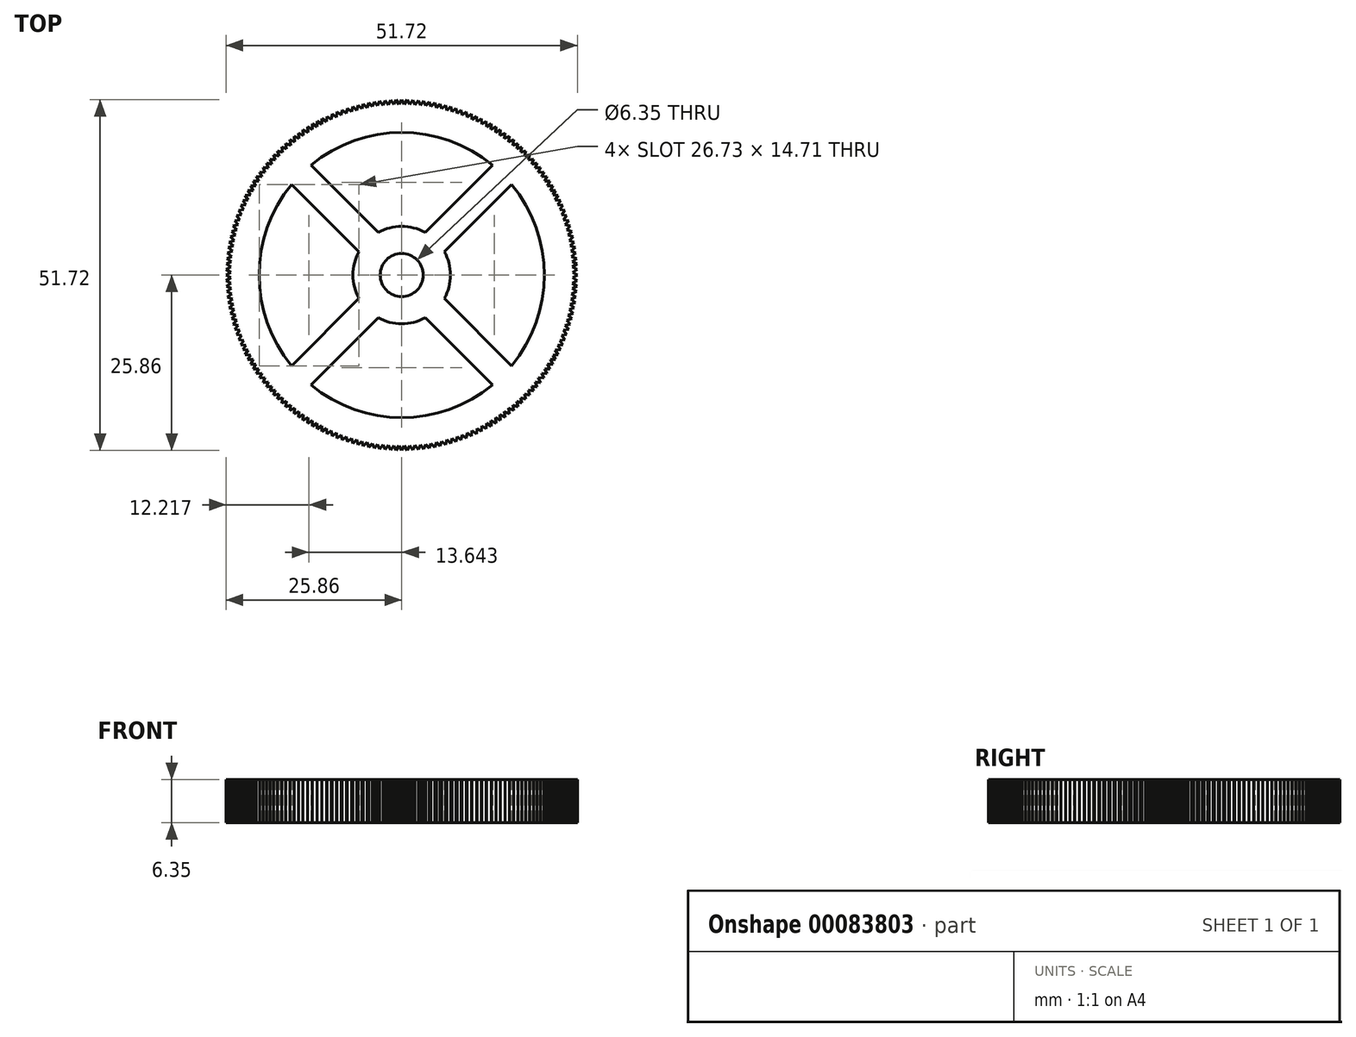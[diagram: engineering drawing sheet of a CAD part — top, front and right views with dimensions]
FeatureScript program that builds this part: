
annotation { "Feature Type Name" : "Feature", "Feature Type Description" : "" }
export const myFeature = defineFeature(function(context is Context, id is Id, definition is map)
    precondition{}
    {
        {
            var Q0;
            Q0=qCreatedBy(makeId("Top.planeOp"),FACE);
            var sketch = newSketch(context, id + "F0", { "sketchPlane" : qUnion([Q0])});
            skCircle(sketch, "E0", {"center": v(0, 0) * mm, "radius": 3.17 * mm});
            skCircle(sketch, "E1", {"center": v(0, 0) * mm, "radius": 25 * mm, "construction": true});
            skLineSegment(sketch, "E2", {"start": v(-3.46, -6.29) * mm, "end": v(-13.37, -16.2) * mm});
            skLineSegment(sketch, "E3", {"start": v(3.46, -6.29) * mm, "end": v(13.37, -16.2) * mm});
            skCircle(sketch, "E4", {"center": v(0, 0) * mm, "radius": 7.17 * mm});
            skCircle(sketch, "E5", {"center": v(0, 0) * mm, "radius": 21 * mm});
            skLineSegment(sketch, "E6.1.0", {"start": v(6.29, 3.46) * mm, "end": v(16.2, 13.37) * mm});
            skLineSegment(sketch, "E6.1.1", {"start": v(6.29, -3.46) * mm, "end": v(16.2, -13.37) * mm});
            skLineSegment(sketch, "E6.2.0", {"start": v(-3.46, 6.29) * mm, "end": v(-13.37, 16.2) * mm});
            skLineSegment(sketch, "E6.2.1", {"start": v(3.46, 6.29) * mm, "end": v(13.37, 16.2) * mm});
            skLineSegment(sketch, "E6.3.0", {"start": v(-6.29, -3.46) * mm, "end": v(-16.2, -13.37) * mm});
            skLineSegment(sketch, "E6.3.1", {"start": v(-6.29, 3.46) * mm, "end": v(-16.2, 13.37) * mm});
            skLineSegment(sketch, "E7", {"start": v(0, -27.54) * mm, "end": v(0, 30.18) * mm, "construction": true});
            skLineSegment(sketch, "E8", {"start": v(-0.5, -25) * mm, "end": v(0, -25.86) * mm});
            skLineSegment(sketch, "E9", {"start": v(0, -25.86) * mm, "end": v(0.5, -25) * mm});
            skLineSegment(sketch, "E10", {"start": v(-0.5, -25) * mm, "end": v(0.5, -25) * mm, "construction": true});
            skLineSegment(sketch, "E11.1.0", {"start": v(0.81, -25.85) * mm, "end": v(1.28, -24.97) * mm});
            skLineSegment(sketch, "E11.1.1", {"start": v(0.29, -25) * mm, "end": v(0.81, -25.85) * mm});
            skLineSegment(sketch, "E11.2.0", {"start": v(1.62, -25.8) * mm, "end": v(2.07, -24.91) * mm});
            skLineSegment(sketch, "E11.2.1", {"start": v(1.07, -24.98) * mm, "end": v(1.62, -25.8) * mm});
            skLineSegment(sketch, "E11.3.0", {"start": v(2.43, -25.75) * mm, "end": v(2.85, -24.84) * mm});
            skLineSegment(sketch, "E11.3.1", {"start": v(1.85, -24.93) * mm, "end": v(2.43, -25.75) * mm});
            skLineSegment(sketch, "E11.4.0", {"start": v(3.24, -25.66) * mm, "end": v(3.63, -24.74) * mm});
            skLineSegment(sketch, "E11.4.1", {"start": v(2.64, -24.86) * mm, "end": v(3.24, -25.66) * mm});
            skLineSegment(sketch, "E11.5.0", {"start": v(4.05, -25.54) * mm, "end": v(4.4, -24.6) * mm});
            skLineSegment(sketch, "E11.5.1", {"start": v(3.42, -24.77) * mm, "end": v(4.05, -25.54) * mm});
            skLineSegment(sketch, "E11.6.0", {"start": v(4.85, -25.4) * mm, "end": v(5.17, -24.46) * mm});
            skLineSegment(sketch, "E11.6.1", {"start": v(4.2, -24.65) * mm, "end": v(4.85, -25.4) * mm});
            skLineSegment(sketch, "E11.7.0", {"start": v(5.64, -25.24) * mm, "end": v(5.94, -24.28) * mm});
            skLineSegment(sketch, "E11.7.1", {"start": v(4.96, -24.5) * mm, "end": v(5.64, -25.24) * mm});
            skLineSegment(sketch, "E11.8.0", {"start": v(6.43, -25.05) * mm, "end": v(6.7, -24.09) * mm});
            skLineSegment(sketch, "E11.8.1", {"start": v(5.73, -24.33) * mm, "end": v(6.43, -25.05) * mm});
            skLineSegment(sketch, "E11.9.0", {"start": v(7.21, -24.83) * mm, "end": v(7.45, -23.86) * mm});
            skLineSegment(sketch, "E11.9.1", {"start": v(6.5, -24.14) * mm, "end": v(7.21, -24.83) * mm});
            skLineSegment(sketch, "E11.10.0", {"start": v(8, -24.6) * mm, "end": v(8.2, -23.62) * mm});
            skLineSegment(sketch, "E11.10.1", {"start": v(7.25, -23.93) * mm, "end": v(8, -24.6) * mm});
            skLineSegment(sketch, "E11.11.0", {"start": v(8.76, -24.33) * mm, "end": v(8.94, -23.35) * mm});
            skLineSegment(sketch, "E11.11.1", {"start": v(8, -23.69) * mm, "end": v(8.76, -24.33) * mm});
            skLineSegment(sketch, "E11.12.0", {"start": v(9.52, -24.04) * mm, "end": v(9.67, -23.06) * mm});
            skLineSegment(sketch, "E11.12.1", {"start": v(8.74, -23.42) * mm, "end": v(9.52, -24.04) * mm});
            skLineSegment(sketch, "E11.13.0", {"start": v(10.27, -23.73) * mm, "end": v(10.39, -22.74) * mm});
            skLineSegment(sketch, "E11.13.1", {"start": v(9.47, -23.14) * mm, "end": v(10.27, -23.73) * mm});
            skLineSegment(sketch, "E11.14.0", {"start": v(11.01, -23.4) * mm, "end": v(11.1, -22.4) * mm});
            skLineSegment(sketch, "E11.14.1", {"start": v(10.19, -22.83) * mm, "end": v(11.01, -23.4) * mm});
            skLineSegment(sketch, "E11.15.0", {"start": v(11.74, -23.04) * mm, "end": v(11.8, -22.04) * mm});
            skLineSegment(sketch, "E11.15.1", {"start": v(10.9, -22.5) * mm, "end": v(11.74, -23.04) * mm});
            skLineSegment(sketch, "E11.16.0", {"start": v(12.46, -22.66) * mm, "end": v(12.48, -21.66) * mm});
            skLineSegment(sketch, "E11.16.1", {"start": v(11.6, -22.14) * mm, "end": v(12.46, -22.66) * mm});
            skLineSegment(sketch, "E11.17.0", {"start": v(13.16, -22.26) * mm, "end": v(13.15, -21.26) * mm});
            skLineSegment(sketch, "E11.17.1", {"start": v(12.3, -21.77) * mm, "end": v(13.16, -22.26) * mm});
            skLineSegment(sketch, "E11.18.0", {"start": v(13.86, -21.84) * mm, "end": v(13.82, -20.84) * mm});
            skLineSegment(sketch, "E11.18.1", {"start": v(12.97, -21.37) * mm, "end": v(13.86, -21.84) * mm});
            skLineSegment(sketch, "E11.19.0", {"start": v(14.54, -21.39) * mm, "end": v(14.46, -20.4) * mm});
            skLineSegment(sketch, "E11.19.1", {"start": v(13.64, -20.95) * mm, "end": v(14.54, -21.39) * mm});
            skLineSegment(sketch, "E11.20.0", {"start": v(15.2, -20.92) * mm, "end": v(15.1, -19.93) * mm});
            skLineSegment(sketch, "E11.20.1", {"start": v(14.29, -20.52) * mm, "end": v(15.2, -20.92) * mm});
            skLineSegment(sketch, "E11.21.0", {"start": v(15.85, -20.43) * mm, "end": v(15.71, -19.44) * mm});
            skLineSegment(sketch, "E11.21.1", {"start": v(14.92, -20.06) * mm, "end": v(15.85, -20.43) * mm});
            skLineSegment(sketch, "E11.22.0", {"start": v(16.48, -19.93) * mm, "end": v(16.32, -18.94) * mm});
            skLineSegment(sketch, "E11.22.1", {"start": v(15.55, -19.58) * mm, "end": v(16.48, -19.93) * mm});
            skLineSegment(sketch, "E11.23.0", {"start": v(17.1, -19.4) * mm, "end": v(16.9, -18.42) * mm});
            skLineSegment(sketch, "E11.23.1", {"start": v(16.15, -19.08) * mm, "end": v(17.1, -19.4) * mm});
            skLineSegment(sketch, "E11.24.0", {"start": v(17.7, -18.85) * mm, "end": v(17.47, -17.88) * mm});
            skLineSegment(sketch, "E11.24.1", {"start": v(16.75, -18.56) * mm, "end": v(17.7, -18.85) * mm});
            skLineSegment(sketch, "E11.25.0", {"start": v(18.29, -18.29) * mm, "end": v(18.03, -17.32) * mm});
            skLineSegment(sketch, "E11.25.1", {"start": v(17.32, -18.03) * mm, "end": v(18.29, -18.29) * mm});
            skLineSegment(sketch, "E11.26.0", {"start": v(18.85, -17.7) * mm, "end": v(18.56, -16.75) * mm});
            skLineSegment(sketch, "E11.26.1", {"start": v(17.88, -17.47) * mm, "end": v(18.85, -17.7) * mm});
            skLineSegment(sketch, "E11.27.0", {"start": v(19.4, -17.1) * mm, "end": v(19.08, -16.15) * mm});
            skLineSegment(sketch, "E11.27.1", {"start": v(18.42, -16.9) * mm, "end": v(19.4, -17.1) * mm});
            skLineSegment(sketch, "E11.28.0", {"start": v(19.93, -16.48) * mm, "end": v(19.58, -15.55) * mm});
            skLineSegment(sketch, "E11.28.1", {"start": v(18.94, -16.32) * mm, "end": v(19.93, -16.48) * mm});
            skLineSegment(sketch, "E11.29.0", {"start": v(20.43, -15.85) * mm, "end": v(20.06, -14.92) * mm});
            skLineSegment(sketch, "E11.29.1", {"start": v(19.44, -15.71) * mm, "end": v(20.43, -15.85) * mm});
            skLineSegment(sketch, "E11.30.0", {"start": v(20.92, -15.2) * mm, "end": v(20.52, -14.29) * mm});
            skLineSegment(sketch, "E11.30.1", {"start": v(19.93, -15.1) * mm, "end": v(20.92, -15.2) * mm});
            skLineSegment(sketch, "E11.31.0", {"start": v(21.39, -14.54) * mm, "end": v(20.95, -13.64) * mm});
            skLineSegment(sketch, "E11.31.1", {"start": v(20.4, -14.46) * mm, "end": v(21.39, -14.54) * mm});
            skLineSegment(sketch, "E11.32.0", {"start": v(21.84, -13.86) * mm, "end": v(21.37, -12.97) * mm});
            skLineSegment(sketch, "E11.32.1", {"start": v(20.84, -13.82) * mm, "end": v(21.84, -13.86) * mm});
            skLineSegment(sketch, "E11.33.0", {"start": v(22.26, -13.16) * mm, "end": v(21.77, -12.3) * mm});
            skLineSegment(sketch, "E11.33.1", {"start": v(21.26, -13.15) * mm, "end": v(22.26, -13.16) * mm});
            skLineSegment(sketch, "E11.34.0", {"start": v(22.66, -12.46) * mm, "end": v(22.14, -11.6) * mm});
            skLineSegment(sketch, "E11.34.1", {"start": v(21.66, -12.48) * mm, "end": v(22.66, -12.46) * mm});
            skLineSegment(sketch, "E11.35.0", {"start": v(23.04, -11.74) * mm, "end": v(22.5, -10.9) * mm});
            skLineSegment(sketch, "E11.35.1", {"start": v(22.04, -11.8) * mm, "end": v(23.04, -11.74) * mm});
            skLineSegment(sketch, "E11.36.0", {"start": v(23.4, -11.01) * mm, "end": v(22.83, -10.19) * mm});
            skLineSegment(sketch, "E11.36.1", {"start": v(22.4, -11.1) * mm, "end": v(23.4, -11.01) * mm});
            skLineSegment(sketch, "E11.37.0", {"start": v(23.73, -10.27) * mm, "end": v(23.14, -9.47) * mm});
            skLineSegment(sketch, "E11.37.1", {"start": v(22.74, -10.39) * mm, "end": v(23.73, -10.27) * mm});
            skLineSegment(sketch, "E11.38.0", {"start": v(24.04, -9.52) * mm, "end": v(23.42, -8.74) * mm});
            skLineSegment(sketch, "E11.38.1", {"start": v(23.06, -9.67) * mm, "end": v(24.04, -9.52) * mm});
            skLineSegment(sketch, "E11.39.0", {"start": v(24.33, -8.76) * mm, "end": v(23.69, -8) * mm});
            skLineSegment(sketch, "E11.39.1", {"start": v(23.35, -8.94) * mm, "end": v(24.33, -8.76) * mm});
            skLineSegment(sketch, "E11.40.0", {"start": v(24.6, -8) * mm, "end": v(23.93, -7.25) * mm});
            skLineSegment(sketch, "E11.40.1", {"start": v(23.62, -8.2) * mm, "end": v(24.6, -8) * mm});
            skLineSegment(sketch, "E11.41.0", {"start": v(24.83, -7.21) * mm, "end": v(24.14, -6.5) * mm});
            skLineSegment(sketch, "E11.41.1", {"start": v(23.86, -7.45) * mm, "end": v(24.83, -7.21) * mm});
            skLineSegment(sketch, "E11.42.0", {"start": v(25.05, -6.43) * mm, "end": v(24.33, -5.73) * mm});
            skLineSegment(sketch, "E11.42.1", {"start": v(24.09, -6.7) * mm, "end": v(25.05, -6.43) * mm});
            skLineSegment(sketch, "E11.43.0", {"start": v(25.24, -5.64) * mm, "end": v(24.5, -4.96) * mm});
            skLineSegment(sketch, "E11.43.1", {"start": v(24.28, -5.94) * mm, "end": v(25.24, -5.64) * mm});
            skLineSegment(sketch, "E11.44.0", {"start": v(25.4, -4.85) * mm, "end": v(24.65, -4.2) * mm});
            skLineSegment(sketch, "E11.44.1", {"start": v(24.46, -5.17) * mm, "end": v(25.4, -4.85) * mm});
            skLineSegment(sketch, "E11.45.0", {"start": v(25.54, -4.05) * mm, "end": v(24.77, -3.42) * mm});
            skLineSegment(sketch, "E11.45.1", {"start": v(24.6, -4.4) * mm, "end": v(25.54, -4.05) * mm});
            skLineSegment(sketch, "E11.46.0", {"start": v(25.66, -3.24) * mm, "end": v(24.86, -2.64) * mm});
            skLineSegment(sketch, "E11.46.1", {"start": v(24.74, -3.63) * mm, "end": v(25.66, -3.24) * mm});
            skLineSegment(sketch, "E11.47.0", {"start": v(25.75, -2.43) * mm, "end": v(24.93, -1.85) * mm});
            skLineSegment(sketch, "E11.47.1", {"start": v(24.84, -2.85) * mm, "end": v(25.75, -2.43) * mm});
            skLineSegment(sketch, "E11.48.0", {"start": v(25.8, -1.62) * mm, "end": v(24.98, -1.07) * mm});
            skLineSegment(sketch, "E11.48.1", {"start": v(24.91, -2.07) * mm, "end": v(25.8, -1.62) * mm});
            skLineSegment(sketch, "E11.49.0", {"start": v(25.85, -0.81) * mm, "end": v(25, -0.29) * mm});
            skLineSegment(sketch, "E11.49.1", {"start": v(24.97, -1.28) * mm, "end": v(25.85, -0.81) * mm});
            skLineSegment(sketch, "E11.50.0", {"start": v(25.86, 0) * mm, "end": v(25, 0.5) * mm});
            skLineSegment(sketch, "E11.50.1", {"start": v(25, -0.5) * mm, "end": v(25.86, 0) * mm});
            skLineSegment(sketch, "E11.51.0", {"start": v(25.85, 0.81) * mm, "end": v(24.97, 1.28) * mm});
            skLineSegment(sketch, "E11.51.1", {"start": v(25, 0.29) * mm, "end": v(25.85, 0.81) * mm});
            skLineSegment(sketch, "E11.52.0", {"start": v(25.8, 1.62) * mm, "end": v(24.91, 2.07) * mm});
            skLineSegment(sketch, "E11.52.1", {"start": v(24.98, 1.07) * mm, "end": v(25.8, 1.62) * mm});
            skLineSegment(sketch, "E11.53.0", {"start": v(25.75, 2.43) * mm, "end": v(24.84, 2.85) * mm});
            skLineSegment(sketch, "E11.53.1", {"start": v(24.93, 1.85) * mm, "end": v(25.75, 2.43) * mm});
            skLineSegment(sketch, "E11.54.0", {"start": v(25.66, 3.24) * mm, "end": v(24.74, 3.63) * mm});
            skLineSegment(sketch, "E11.54.1", {"start": v(24.86, 2.64) * mm, "end": v(25.66, 3.24) * mm});
            skLineSegment(sketch, "E11.55.0", {"start": v(25.54, 4.05) * mm, "end": v(24.6, 4.4) * mm});
            skLineSegment(sketch, "E11.55.1", {"start": v(24.77, 3.42) * mm, "end": v(25.54, 4.05) * mm});
            skLineSegment(sketch, "E11.56.0", {"start": v(25.4, 4.85) * mm, "end": v(24.46, 5.17) * mm});
            skLineSegment(sketch, "E11.56.1", {"start": v(24.65, 4.2) * mm, "end": v(25.4, 4.85) * mm});
            skLineSegment(sketch, "E11.57.0", {"start": v(25.24, 5.64) * mm, "end": v(24.28, 5.94) * mm});
            skLineSegment(sketch, "E11.57.1", {"start": v(24.5, 4.96) * mm, "end": v(25.24, 5.64) * mm});
            skLineSegment(sketch, "E11.58.0", {"start": v(25.05, 6.43) * mm, "end": v(24.09, 6.7) * mm});
            skLineSegment(sketch, "E11.58.1", {"start": v(24.33, 5.73) * mm, "end": v(25.05, 6.43) * mm});
            skLineSegment(sketch, "E11.59.0", {"start": v(24.83, 7.21) * mm, "end": v(23.86, 7.45) * mm});
            skLineSegment(sketch, "E11.59.1", {"start": v(24.14, 6.5) * mm, "end": v(24.83, 7.21) * mm});
            skLineSegment(sketch, "E11.60.0", {"start": v(24.6, 8) * mm, "end": v(23.62, 8.2) * mm});
            skLineSegment(sketch, "E11.60.1", {"start": v(23.93, 7.25) * mm, "end": v(24.6, 8) * mm});
            skLineSegment(sketch, "E11.61.0", {"start": v(24.33, 8.76) * mm, "end": v(23.35, 8.94) * mm});
            skLineSegment(sketch, "E11.61.1", {"start": v(23.69, 8) * mm, "end": v(24.33, 8.76) * mm});
            skLineSegment(sketch, "E11.62.0", {"start": v(24.04, 9.52) * mm, "end": v(23.06, 9.67) * mm});
            skLineSegment(sketch, "E11.62.1", {"start": v(23.42, 8.74) * mm, "end": v(24.04, 9.52) * mm});
            skLineSegment(sketch, "E11.63.0", {"start": v(23.73, 10.27) * mm, "end": v(22.74, 10.39) * mm});
            skLineSegment(sketch, "E11.63.1", {"start": v(23.14, 9.47) * mm, "end": v(23.73, 10.27) * mm});
            skLineSegment(sketch, "E11.64.0", {"start": v(23.4, 11.01) * mm, "end": v(22.4, 11.1) * mm});
            skLineSegment(sketch, "E11.64.1", {"start": v(22.83, 10.19) * mm, "end": v(23.4, 11.01) * mm});
            skLineSegment(sketch, "E11.65.0", {"start": v(23.04, 11.74) * mm, "end": v(22.04, 11.8) * mm});
            skLineSegment(sketch, "E11.65.1", {"start": v(22.5, 10.9) * mm, "end": v(23.04, 11.74) * mm});
            skLineSegment(sketch, "E11.66.0", {"start": v(22.66, 12.46) * mm, "end": v(21.66, 12.48) * mm});
            skLineSegment(sketch, "E11.66.1", {"start": v(22.14, 11.6) * mm, "end": v(22.66, 12.46) * mm});
            skLineSegment(sketch, "E11.67.0", {"start": v(22.26, 13.16) * mm, "end": v(21.26, 13.15) * mm});
            skLineSegment(sketch, "E11.67.1", {"start": v(21.77, 12.3) * mm, "end": v(22.26, 13.16) * mm});
            skLineSegment(sketch, "E11.68.0", {"start": v(21.84, 13.86) * mm, "end": v(20.84, 13.82) * mm});
            skLineSegment(sketch, "E11.68.1", {"start": v(21.37, 12.97) * mm, "end": v(21.84, 13.86) * mm});
            skLineSegment(sketch, "E11.69.0", {"start": v(21.39, 14.54) * mm, "end": v(20.4, 14.46) * mm});
            skLineSegment(sketch, "E11.69.1", {"start": v(20.95, 13.64) * mm, "end": v(21.39, 14.54) * mm});
            skLineSegment(sketch, "E11.70.0", {"start": v(20.92, 15.2) * mm, "end": v(19.93, 15.1) * mm});
            skLineSegment(sketch, "E11.70.1", {"start": v(20.52, 14.29) * mm, "end": v(20.92, 15.2) * mm});
            skLineSegment(sketch, "E11.71.0", {"start": v(20.43, 15.85) * mm, "end": v(19.44, 15.71) * mm});
            skLineSegment(sketch, "E11.71.1", {"start": v(20.06, 14.92) * mm, "end": v(20.43, 15.85) * mm});
            skLineSegment(sketch, "E11.72.0", {"start": v(19.93, 16.48) * mm, "end": v(18.94, 16.32) * mm});
            skLineSegment(sketch, "E11.72.1", {"start": v(19.58, 15.55) * mm, "end": v(19.93, 16.48) * mm});
            skLineSegment(sketch, "E11.73.0", {"start": v(19.4, 17.1) * mm, "end": v(18.42, 16.9) * mm});
            skLineSegment(sketch, "E11.73.1", {"start": v(19.08, 16.15) * mm, "end": v(19.4, 17.1) * mm});
            skLineSegment(sketch, "E11.74.0", {"start": v(18.85, 17.7) * mm, "end": v(17.88, 17.47) * mm});
            skLineSegment(sketch, "E11.74.1", {"start": v(18.56, 16.75) * mm, "end": v(18.85, 17.7) * mm});
            skLineSegment(sketch, "E11.75.0", {"start": v(18.29, 18.29) * mm, "end": v(17.32, 18.03) * mm});
            skLineSegment(sketch, "E11.75.1", {"start": v(18.03, 17.32) * mm, "end": v(18.29, 18.29) * mm});
            skLineSegment(sketch, "E11.76.0", {"start": v(17.7, 18.85) * mm, "end": v(16.75, 18.56) * mm});
            skLineSegment(sketch, "E11.76.1", {"start": v(17.47, 17.88) * mm, "end": v(17.7, 18.85) * mm});
            skLineSegment(sketch, "E11.77.0", {"start": v(17.1, 19.4) * mm, "end": v(16.15, 19.08) * mm});
            skLineSegment(sketch, "E11.77.1", {"start": v(16.9, 18.42) * mm, "end": v(17.1, 19.4) * mm});
            skLineSegment(sketch, "E11.78.0", {"start": v(16.48, 19.93) * mm, "end": v(15.55, 19.58) * mm});
            skLineSegment(sketch, "E11.78.1", {"start": v(16.32, 18.94) * mm, "end": v(16.48, 19.93) * mm});
            skLineSegment(sketch, "E11.79.0", {"start": v(15.85, 20.43) * mm, "end": v(14.92, 20.06) * mm});
            skLineSegment(sketch, "E11.79.1", {"start": v(15.71, 19.44) * mm, "end": v(15.85, 20.43) * mm});
            skLineSegment(sketch, "E11.80.0", {"start": v(15.2, 20.92) * mm, "end": v(14.29, 20.52) * mm});
            skLineSegment(sketch, "E11.80.1", {"start": v(15.1, 19.93) * mm, "end": v(15.2, 20.92) * mm});
            skLineSegment(sketch, "E11.81.0", {"start": v(14.54, 21.39) * mm, "end": v(13.64, 20.95) * mm});
            skLineSegment(sketch, "E11.81.1", {"start": v(14.46, 20.4) * mm, "end": v(14.54, 21.39) * mm});
            skLineSegment(sketch, "E11.82.0", {"start": v(13.86, 21.84) * mm, "end": v(12.97, 21.37) * mm});
            skLineSegment(sketch, "E11.82.1", {"start": v(13.82, 20.84) * mm, "end": v(13.86, 21.84) * mm});
            skLineSegment(sketch, "E11.83.0", {"start": v(13.16, 22.26) * mm, "end": v(12.3, 21.77) * mm});
            skLineSegment(sketch, "E11.83.1", {"start": v(13.15, 21.26) * mm, "end": v(13.16, 22.26) * mm});
            skLineSegment(sketch, "E11.84.0", {"start": v(12.46, 22.66) * mm, "end": v(11.6, 22.14) * mm});
            skLineSegment(sketch, "E11.84.1", {"start": v(12.48, 21.66) * mm, "end": v(12.46, 22.66) * mm});
            skLineSegment(sketch, "E11.85.0", {"start": v(11.74, 23.04) * mm, "end": v(10.9, 22.5) * mm});
            skLineSegment(sketch, "E11.85.1", {"start": v(11.8, 22.04) * mm, "end": v(11.74, 23.04) * mm});
            skLineSegment(sketch, "E11.86.0", {"start": v(11.01, 23.4) * mm, "end": v(10.19, 22.83) * mm});
            skLineSegment(sketch, "E11.86.1", {"start": v(11.1, 22.4) * mm, "end": v(11.01, 23.4) * mm});
            skLineSegment(sketch, "E11.87.0", {"start": v(10.27, 23.73) * mm, "end": v(9.47, 23.14) * mm});
            skLineSegment(sketch, "E11.87.1", {"start": v(10.39, 22.74) * mm, "end": v(10.27, 23.73) * mm});
            skLineSegment(sketch, "E11.88.0", {"start": v(9.52, 24.04) * mm, "end": v(8.74, 23.42) * mm});
            skLineSegment(sketch, "E11.88.1", {"start": v(9.67, 23.06) * mm, "end": v(9.52, 24.04) * mm});
            skLineSegment(sketch, "E11.89.0", {"start": v(8.76, 24.33) * mm, "end": v(8, 23.69) * mm});
            skLineSegment(sketch, "E11.89.1", {"start": v(8.94, 23.35) * mm, "end": v(8.76, 24.33) * mm});
            skLineSegment(sketch, "E11.90.0", {"start": v(8, 24.6) * mm, "end": v(7.25, 23.93) * mm});
            skLineSegment(sketch, "E11.90.1", {"start": v(8.2, 23.62) * mm, "end": v(8, 24.6) * mm});
            skLineSegment(sketch, "E11.91.0", {"start": v(7.21, 24.83) * mm, "end": v(6.5, 24.14) * mm});
            skLineSegment(sketch, "E11.91.1", {"start": v(7.45, 23.86) * mm, "end": v(7.21, 24.83) * mm});
            skLineSegment(sketch, "E11.92.0", {"start": v(6.43, 25.05) * mm, "end": v(5.73, 24.33) * mm});
            skLineSegment(sketch, "E11.92.1", {"start": v(6.7, 24.09) * mm, "end": v(6.43, 25.05) * mm});
            skLineSegment(sketch, "E11.93.0", {"start": v(5.64, 25.24) * mm, "end": v(4.96, 24.5) * mm});
            skLineSegment(sketch, "E11.93.1", {"start": v(5.94, 24.28) * mm, "end": v(5.64, 25.24) * mm});
            skLineSegment(sketch, "E11.94.0", {"start": v(4.85, 25.4) * mm, "end": v(4.2, 24.65) * mm});
            skLineSegment(sketch, "E11.94.1", {"start": v(5.17, 24.46) * mm, "end": v(4.85, 25.4) * mm});
            skLineSegment(sketch, "E11.95.0", {"start": v(4.05, 25.54) * mm, "end": v(3.42, 24.77) * mm});
            skLineSegment(sketch, "E11.95.1", {"start": v(4.4, 24.6) * mm, "end": v(4.05, 25.54) * mm});
            skLineSegment(sketch, "E11.96.0", {"start": v(3.24, 25.66) * mm, "end": v(2.64, 24.86) * mm});
            skLineSegment(sketch, "E11.96.1", {"start": v(3.63, 24.74) * mm, "end": v(3.24, 25.66) * mm});
            skLineSegment(sketch, "E11.97.0", {"start": v(2.43, 25.75) * mm, "end": v(1.85, 24.93) * mm});
            skLineSegment(sketch, "E11.97.1", {"start": v(2.85, 24.84) * mm, "end": v(2.43, 25.75) * mm});
            skLineSegment(sketch, "E11.98.0", {"start": v(1.62, 25.8) * mm, "end": v(1.07, 24.98) * mm});
            skLineSegment(sketch, "E11.98.1", {"start": v(2.07, 24.91) * mm, "end": v(1.62, 25.8) * mm});
            skLineSegment(sketch, "E11.99.0", {"start": v(0.81, 25.85) * mm, "end": v(0.29, 25) * mm});
            skLineSegment(sketch, "E11.99.1", {"start": v(1.28, 24.97) * mm, "end": v(0.81, 25.85) * mm});
            skLineSegment(sketch, "E11.100.0", {"start": v(0, 25.86) * mm, "end": v(-0.5, 25) * mm});
            skLineSegment(sketch, "E11.100.1", {"start": v(0.5, 25) * mm, "end": v(0, 25.86) * mm});
            skLineSegment(sketch, "E11.101.0", {"start": v(-0.81, 25.85) * mm, "end": v(-1.28, 24.97) * mm});
            skLineSegment(sketch, "E11.101.1", {"start": v(-0.29, 25) * mm, "end": v(-0.81, 25.85) * mm});
            skLineSegment(sketch, "E11.102.0", {"start": v(-1.62, 25.8) * mm, "end": v(-2.07, 24.91) * mm});
            skLineSegment(sketch, "E11.102.1", {"start": v(-1.07, 24.98) * mm, "end": v(-1.62, 25.8) * mm});
            skLineSegment(sketch, "E11.103.0", {"start": v(-2.43, 25.75) * mm, "end": v(-2.85, 24.84) * mm});
            skLineSegment(sketch, "E11.103.1", {"start": v(-1.85, 24.93) * mm, "end": v(-2.43, 25.75) * mm});
            skLineSegment(sketch, "E11.104.0", {"start": v(-3.24, 25.66) * mm, "end": v(-3.63, 24.74) * mm});
            skLineSegment(sketch, "E11.104.1", {"start": v(-2.64, 24.86) * mm, "end": v(-3.24, 25.66) * mm});
            skLineSegment(sketch, "E11.105.0", {"start": v(-4.05, 25.54) * mm, "end": v(-4.4, 24.6) * mm});
            skLineSegment(sketch, "E11.105.1", {"start": v(-3.42, 24.77) * mm, "end": v(-4.05, 25.54) * mm});
            skLineSegment(sketch, "E11.106.0", {"start": v(-4.85, 25.4) * mm, "end": v(-5.17, 24.46) * mm});
            skLineSegment(sketch, "E11.106.1", {"start": v(-4.2, 24.65) * mm, "end": v(-4.85, 25.4) * mm});
            skLineSegment(sketch, "E11.107.0", {"start": v(-5.64, 25.24) * mm, "end": v(-5.94, 24.28) * mm});
            skLineSegment(sketch, "E11.107.1", {"start": v(-4.96, 24.5) * mm, "end": v(-5.64, 25.24) * mm});
            skLineSegment(sketch, "E11.108.0", {"start": v(-6.43, 25.05) * mm, "end": v(-6.7, 24.09) * mm});
            skLineSegment(sketch, "E11.108.1", {"start": v(-5.73, 24.33) * mm, "end": v(-6.43, 25.05) * mm});
            skLineSegment(sketch, "E11.109.0", {"start": v(-7.21, 24.83) * mm, "end": v(-7.45, 23.86) * mm});
            skLineSegment(sketch, "E11.109.1", {"start": v(-6.5, 24.14) * mm, "end": v(-7.21, 24.83) * mm});
            skLineSegment(sketch, "E11.110.0", {"start": v(-8, 24.6) * mm, "end": v(-8.2, 23.62) * mm});
            skLineSegment(sketch, "E11.110.1", {"start": v(-7.25, 23.93) * mm, "end": v(-8, 24.6) * mm});
            skLineSegment(sketch, "E11.111.0", {"start": v(-8.76, 24.33) * mm, "end": v(-8.94, 23.35) * mm});
            skLineSegment(sketch, "E11.111.1", {"start": v(-8, 23.69) * mm, "end": v(-8.76, 24.33) * mm});
            skLineSegment(sketch, "E11.112.0", {"start": v(-9.52, 24.04) * mm, "end": v(-9.67, 23.06) * mm});
            skLineSegment(sketch, "E11.112.1", {"start": v(-8.74, 23.42) * mm, "end": v(-9.52, 24.04) * mm});
            skLineSegment(sketch, "E11.113.0", {"start": v(-10.27, 23.73) * mm, "end": v(-10.39, 22.74) * mm});
            skLineSegment(sketch, "E11.113.1", {"start": v(-9.47, 23.14) * mm, "end": v(-10.27, 23.73) * mm});
            skLineSegment(sketch, "E11.114.0", {"start": v(-11.01, 23.4) * mm, "end": v(-11.1, 22.4) * mm});
            skLineSegment(sketch, "E11.114.1", {"start": v(-10.19, 22.83) * mm, "end": v(-11.01, 23.4) * mm});
            skLineSegment(sketch, "E11.115.0", {"start": v(-11.74, 23.04) * mm, "end": v(-11.8, 22.04) * mm});
            skLineSegment(sketch, "E11.115.1", {"start": v(-10.9, 22.5) * mm, "end": v(-11.74, 23.04) * mm});
            skLineSegment(sketch, "E11.116.0", {"start": v(-12.46, 22.66) * mm, "end": v(-12.48, 21.66) * mm});
            skLineSegment(sketch, "E11.116.1", {"start": v(-11.6, 22.14) * mm, "end": v(-12.46, 22.66) * mm});
            skLineSegment(sketch, "E11.117.0", {"start": v(-13.16, 22.26) * mm, "end": v(-13.15, 21.26) * mm});
            skLineSegment(sketch, "E11.117.1", {"start": v(-12.3, 21.77) * mm, "end": v(-13.16, 22.26) * mm});
            skLineSegment(sketch, "E11.118.0", {"start": v(-13.86, 21.84) * mm, "end": v(-13.82, 20.84) * mm});
            skLineSegment(sketch, "E11.118.1", {"start": v(-12.97, 21.37) * mm, "end": v(-13.86, 21.84) * mm});
            skLineSegment(sketch, "E11.119.0", {"start": v(-14.54, 21.39) * mm, "end": v(-14.46, 20.4) * mm});
            skLineSegment(sketch, "E11.119.1", {"start": v(-13.64, 20.95) * mm, "end": v(-14.54, 21.39) * mm});
            skLineSegment(sketch, "E11.120.0", {"start": v(-15.2, 20.92) * mm, "end": v(-15.1, 19.93) * mm});
            skLineSegment(sketch, "E11.120.1", {"start": v(-14.29, 20.52) * mm, "end": v(-15.2, 20.92) * mm});
            skLineSegment(sketch, "E11.121.0", {"start": v(-15.85, 20.43) * mm, "end": v(-15.71, 19.44) * mm});
            skLineSegment(sketch, "E11.121.1", {"start": v(-14.92, 20.06) * mm, "end": v(-15.85, 20.43) * mm});
            skLineSegment(sketch, "E11.122.0", {"start": v(-16.48, 19.93) * mm, "end": v(-16.32, 18.94) * mm});
            skLineSegment(sketch, "E11.122.1", {"start": v(-15.55, 19.58) * mm, "end": v(-16.48, 19.93) * mm});
            skLineSegment(sketch, "E11.123.0", {"start": v(-17.1, 19.4) * mm, "end": v(-16.9, 18.42) * mm});
            skLineSegment(sketch, "E11.123.1", {"start": v(-16.15, 19.08) * mm, "end": v(-17.1, 19.4) * mm});
            skLineSegment(sketch, "E11.124.0", {"start": v(-17.7, 18.85) * mm, "end": v(-17.47, 17.88) * mm});
            skLineSegment(sketch, "E11.124.1", {"start": v(-16.75, 18.56) * mm, "end": v(-17.7, 18.85) * mm});
            skLineSegment(sketch, "E11.125.0", {"start": v(-18.29, 18.29) * mm, "end": v(-18.03, 17.32) * mm});
            skLineSegment(sketch, "E11.125.1", {"start": v(-17.32, 18.03) * mm, "end": v(-18.29, 18.29) * mm});
            skLineSegment(sketch, "E11.126.0", {"start": v(-18.85, 17.7) * mm, "end": v(-18.56, 16.75) * mm});
            skLineSegment(sketch, "E11.126.1", {"start": v(-17.88, 17.47) * mm, "end": v(-18.85, 17.7) * mm});
            skLineSegment(sketch, "E11.127.0", {"start": v(-19.4, 17.1) * mm, "end": v(-19.08, 16.15) * mm});
            skLineSegment(sketch, "E11.127.1", {"start": v(-18.42, 16.9) * mm, "end": v(-19.4, 17.1) * mm});
            skLineSegment(sketch, "E11.128.0", {"start": v(-19.93, 16.48) * mm, "end": v(-19.58, 15.55) * mm});
            skLineSegment(sketch, "E11.128.1", {"start": v(-18.94, 16.32) * mm, "end": v(-19.93, 16.48) * mm});
            skLineSegment(sketch, "E11.129.0", {"start": v(-20.43, 15.85) * mm, "end": v(-20.06, 14.92) * mm});
            skLineSegment(sketch, "E11.129.1", {"start": v(-19.44, 15.71) * mm, "end": v(-20.43, 15.85) * mm});
            skLineSegment(sketch, "E11.130.0", {"start": v(-20.92, 15.2) * mm, "end": v(-20.52, 14.29) * mm});
            skLineSegment(sketch, "E11.130.1", {"start": v(-19.93, 15.1) * mm, "end": v(-20.92, 15.2) * mm});
            skLineSegment(sketch, "E11.131.0", {"start": v(-21.39, 14.54) * mm, "end": v(-20.95, 13.64) * mm});
            skLineSegment(sketch, "E11.131.1", {"start": v(-20.4, 14.46) * mm, "end": v(-21.39, 14.54) * mm});
            skLineSegment(sketch, "E11.132.0", {"start": v(-21.84, 13.86) * mm, "end": v(-21.37, 12.97) * mm});
            skLineSegment(sketch, "E11.132.1", {"start": v(-20.84, 13.82) * mm, "end": v(-21.84, 13.86) * mm});
            skLineSegment(sketch, "E11.133.0", {"start": v(-22.26, 13.16) * mm, "end": v(-21.77, 12.3) * mm});
            skLineSegment(sketch, "E11.133.1", {"start": v(-21.26, 13.15) * mm, "end": v(-22.26, 13.16) * mm});
            skLineSegment(sketch, "E11.134.0", {"start": v(-22.66, 12.46) * mm, "end": v(-22.14, 11.6) * mm});
            skLineSegment(sketch, "E11.134.1", {"start": v(-21.66, 12.48) * mm, "end": v(-22.66, 12.46) * mm});
            skLineSegment(sketch, "E11.135.0", {"start": v(-23.04, 11.74) * mm, "end": v(-22.5, 10.9) * mm});
            skLineSegment(sketch, "E11.135.1", {"start": v(-22.04, 11.8) * mm, "end": v(-23.04, 11.74) * mm});
            skLineSegment(sketch, "E11.136.0", {"start": v(-23.4, 11.01) * mm, "end": v(-22.83, 10.19) * mm});
            skLineSegment(sketch, "E11.136.1", {"start": v(-22.4, 11.1) * mm, "end": v(-23.4, 11.01) * mm});
            skLineSegment(sketch, "E11.137.0", {"start": v(-23.73, 10.27) * mm, "end": v(-23.14, 9.47) * mm});
            skLineSegment(sketch, "E11.137.1", {"start": v(-22.74, 10.39) * mm, "end": v(-23.73, 10.27) * mm});
            skLineSegment(sketch, "E11.138.0", {"start": v(-24.04, 9.52) * mm, "end": v(-23.42, 8.74) * mm});
            skLineSegment(sketch, "E11.138.1", {"start": v(-23.06, 9.67) * mm, "end": v(-24.04, 9.52) * mm});
            skLineSegment(sketch, "E11.139.0", {"start": v(-24.33, 8.76) * mm, "end": v(-23.69, 8) * mm});
            skLineSegment(sketch, "E11.139.1", {"start": v(-23.35, 8.94) * mm, "end": v(-24.33, 8.76) * mm});
            skLineSegment(sketch, "E11.140.0", {"start": v(-24.6, 8) * mm, "end": v(-23.93, 7.25) * mm});
            skLineSegment(sketch, "E11.140.1", {"start": v(-23.62, 8.2) * mm, "end": v(-24.6, 8) * mm});
            skLineSegment(sketch, "E11.141.0", {"start": v(-24.83, 7.21) * mm, "end": v(-24.14, 6.5) * mm});
            skLineSegment(sketch, "E11.141.1", {"start": v(-23.86, 7.45) * mm, "end": v(-24.83, 7.21) * mm});
            skLineSegment(sketch, "E11.142.0", {"start": v(-25.05, 6.43) * mm, "end": v(-24.33, 5.73) * mm});
            skLineSegment(sketch, "E11.142.1", {"start": v(-24.09, 6.7) * mm, "end": v(-25.05, 6.43) * mm});
            skLineSegment(sketch, "E11.143.0", {"start": v(-25.24, 5.64) * mm, "end": v(-24.5, 4.96) * mm});
            skLineSegment(sketch, "E11.143.1", {"start": v(-24.28, 5.94) * mm, "end": v(-25.24, 5.64) * mm});
            skLineSegment(sketch, "E11.144.0", {"start": v(-25.4, 4.85) * mm, "end": v(-24.65, 4.2) * mm});
            skLineSegment(sketch, "E11.144.1", {"start": v(-24.46, 5.17) * mm, "end": v(-25.4, 4.85) * mm});
            skLineSegment(sketch, "E11.145.0", {"start": v(-25.54, 4.05) * mm, "end": v(-24.77, 3.42) * mm});
            skLineSegment(sketch, "E11.145.1", {"start": v(-24.6, 4.4) * mm, "end": v(-25.54, 4.05) * mm});
            skLineSegment(sketch, "E11.146.0", {"start": v(-25.66, 3.24) * mm, "end": v(-24.86, 2.64) * mm});
            skLineSegment(sketch, "E11.146.1", {"start": v(-24.74, 3.63) * mm, "end": v(-25.66, 3.24) * mm});
            skLineSegment(sketch, "E11.147.0", {"start": v(-25.75, 2.43) * mm, "end": v(-24.93, 1.85) * mm});
            skLineSegment(sketch, "E11.147.1", {"start": v(-24.84, 2.85) * mm, "end": v(-25.75, 2.43) * mm});
            skLineSegment(sketch, "E11.148.0", {"start": v(-25.8, 1.62) * mm, "end": v(-24.98, 1.07) * mm});
            skLineSegment(sketch, "E11.148.1", {"start": v(-24.91, 2.07) * mm, "end": v(-25.8, 1.62) * mm});
            skLineSegment(sketch, "E11.149.0", {"start": v(-25.85, 0.81) * mm, "end": v(-25, 0.29) * mm});
            skLineSegment(sketch, "E11.149.1", {"start": v(-24.97, 1.28) * mm, "end": v(-25.85, 0.81) * mm});
            skLineSegment(sketch, "E11.150.0", {"start": v(-25.86, 0) * mm, "end": v(-25, -0.5) * mm});
            skLineSegment(sketch, "E11.150.1", {"start": v(-25, 0.5) * mm, "end": v(-25.86, 0) * mm});
            skLineSegment(sketch, "E11.151.0", {"start": v(-25.85, -0.81) * mm, "end": v(-24.97, -1.28) * mm});
            skLineSegment(sketch, "E11.151.1", {"start": v(-25, -0.29) * mm, "end": v(-25.85, -0.81) * mm});
            skLineSegment(sketch, "E11.152.0", {"start": v(-25.8, -1.62) * mm, "end": v(-24.91, -2.07) * mm});
            skLineSegment(sketch, "E11.152.1", {"start": v(-24.98, -1.07) * mm, "end": v(-25.8, -1.62) * mm});
            skLineSegment(sketch, "E11.153.0", {"start": v(-25.75, -2.43) * mm, "end": v(-24.84, -2.85) * mm});
            skLineSegment(sketch, "E11.153.1", {"start": v(-24.93, -1.85) * mm, "end": v(-25.75, -2.43) * mm});
            skLineSegment(sketch, "E11.154.0", {"start": v(-25.66, -3.24) * mm, "end": v(-24.74, -3.63) * mm});
            skLineSegment(sketch, "E11.154.1", {"start": v(-24.86, -2.64) * mm, "end": v(-25.66, -3.24) * mm});
            skLineSegment(sketch, "E11.155.0", {"start": v(-25.54, -4.05) * mm, "end": v(-24.6, -4.4) * mm});
            skLineSegment(sketch, "E11.155.1", {"start": v(-24.77, -3.42) * mm, "end": v(-25.54, -4.05) * mm});
            skLineSegment(sketch, "E11.156.0", {"start": v(-25.4, -4.85) * mm, "end": v(-24.46, -5.17) * mm});
            skLineSegment(sketch, "E11.156.1", {"start": v(-24.65, -4.2) * mm, "end": v(-25.4, -4.85) * mm});
            skLineSegment(sketch, "E11.157.0", {"start": v(-25.24, -5.64) * mm, "end": v(-24.28, -5.94) * mm});
            skLineSegment(sketch, "E11.157.1", {"start": v(-24.5, -4.96) * mm, "end": v(-25.24, -5.64) * mm});
            skLineSegment(sketch, "E11.158.0", {"start": v(-25.05, -6.43) * mm, "end": v(-24.09, -6.7) * mm});
            skLineSegment(sketch, "E11.158.1", {"start": v(-24.33, -5.73) * mm, "end": v(-25.05, -6.43) * mm});
            skLineSegment(sketch, "E11.159.0", {"start": v(-24.83, -7.21) * mm, "end": v(-23.86, -7.45) * mm});
            skLineSegment(sketch, "E11.159.1", {"start": v(-24.14, -6.5) * mm, "end": v(-24.83, -7.21) * mm});
            skLineSegment(sketch, "E11.160.0", {"start": v(-24.6, -8) * mm, "end": v(-23.62, -8.2) * mm});
            skLineSegment(sketch, "E11.160.1", {"start": v(-23.93, -7.25) * mm, "end": v(-24.6, -8) * mm});
            skLineSegment(sketch, "E11.161.0", {"start": v(-24.33, -8.76) * mm, "end": v(-23.35, -8.94) * mm});
            skLineSegment(sketch, "E11.161.1", {"start": v(-23.69, -8) * mm, "end": v(-24.33, -8.76) * mm});
            skLineSegment(sketch, "E11.162.0", {"start": v(-24.04, -9.52) * mm, "end": v(-23.06, -9.67) * mm});
            skLineSegment(sketch, "E11.162.1", {"start": v(-23.42, -8.74) * mm, "end": v(-24.04, -9.52) * mm});
            skLineSegment(sketch, "E11.163.0", {"start": v(-23.73, -10.27) * mm, "end": v(-22.74, -10.39) * mm});
            skLineSegment(sketch, "E11.163.1", {"start": v(-23.14, -9.47) * mm, "end": v(-23.73, -10.27) * mm});
            skLineSegment(sketch, "E11.164.0", {"start": v(-23.4, -11.01) * mm, "end": v(-22.4, -11.1) * mm});
            skLineSegment(sketch, "E11.164.1", {"start": v(-22.83, -10.19) * mm, "end": v(-23.4, -11.01) * mm});
            skLineSegment(sketch, "E11.165.0", {"start": v(-23.04, -11.74) * mm, "end": v(-22.04, -11.8) * mm});
            skLineSegment(sketch, "E11.165.1", {"start": v(-22.5, -10.9) * mm, "end": v(-23.04, -11.74) * mm});
            skLineSegment(sketch, "E11.166.0", {"start": v(-22.66, -12.46) * mm, "end": v(-21.66, -12.48) * mm});
            skLineSegment(sketch, "E11.166.1", {"start": v(-22.14, -11.6) * mm, "end": v(-22.66, -12.46) * mm});
            skLineSegment(sketch, "E11.167.0", {"start": v(-22.26, -13.16) * mm, "end": v(-21.26, -13.15) * mm});
            skLineSegment(sketch, "E11.167.1", {"start": v(-21.77, -12.3) * mm, "end": v(-22.26, -13.16) * mm});
            skLineSegment(sketch, "E11.168.0", {"start": v(-21.84, -13.86) * mm, "end": v(-20.84, -13.82) * mm});
            skLineSegment(sketch, "E11.168.1", {"start": v(-21.37, -12.97) * mm, "end": v(-21.84, -13.86) * mm});
            skLineSegment(sketch, "E11.169.0", {"start": v(-21.39, -14.54) * mm, "end": v(-20.4, -14.46) * mm});
            skLineSegment(sketch, "E11.169.1", {"start": v(-20.95, -13.64) * mm, "end": v(-21.39, -14.54) * mm});
            skLineSegment(sketch, "E11.170.0", {"start": v(-20.92, -15.2) * mm, "end": v(-19.93, -15.1) * mm});
            skLineSegment(sketch, "E11.170.1", {"start": v(-20.52, -14.29) * mm, "end": v(-20.92, -15.2) * mm});
            skLineSegment(sketch, "E11.171.0", {"start": v(-20.43, -15.85) * mm, "end": v(-19.44, -15.71) * mm});
            skLineSegment(sketch, "E11.171.1", {"start": v(-20.06, -14.92) * mm, "end": v(-20.43, -15.85) * mm});
            skLineSegment(sketch, "E11.172.0", {"start": v(-19.93, -16.48) * mm, "end": v(-18.94, -16.32) * mm});
            skLineSegment(sketch, "E11.172.1", {"start": v(-19.58, -15.55) * mm, "end": v(-19.93, -16.48) * mm});
            skLineSegment(sketch, "E11.173.0", {"start": v(-19.4, -17.1) * mm, "end": v(-18.42, -16.9) * mm});
            skLineSegment(sketch, "E11.173.1", {"start": v(-19.08, -16.15) * mm, "end": v(-19.4, -17.1) * mm});
            skLineSegment(sketch, "E11.174.0", {"start": v(-18.85, -17.7) * mm, "end": v(-17.88, -17.47) * mm});
            skLineSegment(sketch, "E11.174.1", {"start": v(-18.56, -16.75) * mm, "end": v(-18.85, -17.7) * mm});
            skLineSegment(sketch, "E11.175.0", {"start": v(-18.29, -18.29) * mm, "end": v(-17.32, -18.03) * mm});
            skLineSegment(sketch, "E11.175.1", {"start": v(-18.03, -17.32) * mm, "end": v(-18.29, -18.29) * mm});
            skLineSegment(sketch, "E11.176.0", {"start": v(-17.7, -18.85) * mm, "end": v(-16.75, -18.56) * mm});
            skLineSegment(sketch, "E11.176.1", {"start": v(-17.47, -17.88) * mm, "end": v(-17.7, -18.85) * mm});
            skLineSegment(sketch, "E11.177.0", {"start": v(-17.1, -19.4) * mm, "end": v(-16.15, -19.08) * mm});
            skLineSegment(sketch, "E11.177.1", {"start": v(-16.9, -18.42) * mm, "end": v(-17.1, -19.4) * mm});
            skLineSegment(sketch, "E11.178.0", {"start": v(-16.48, -19.93) * mm, "end": v(-15.55, -19.58) * mm});
            skLineSegment(sketch, "E11.178.1", {"start": v(-16.32, -18.94) * mm, "end": v(-16.48, -19.93) * mm});
            skLineSegment(sketch, "E11.179.0", {"start": v(-15.85, -20.43) * mm, "end": v(-14.92, -20.06) * mm});
            skLineSegment(sketch, "E11.179.1", {"start": v(-15.71, -19.44) * mm, "end": v(-15.85, -20.43) * mm});
            skLineSegment(sketch, "E11.180.0", {"start": v(-15.2, -20.92) * mm, "end": v(-14.29, -20.52) * mm});
            skLineSegment(sketch, "E11.180.1", {"start": v(-15.1, -19.93) * mm, "end": v(-15.2, -20.92) * mm});
            skLineSegment(sketch, "E11.181.0", {"start": v(-14.54, -21.39) * mm, "end": v(-13.64, -20.95) * mm});
            skLineSegment(sketch, "E11.181.1", {"start": v(-14.46, -20.4) * mm, "end": v(-14.54, -21.39) * mm});
            skLineSegment(sketch, "E11.182.0", {"start": v(-13.86, -21.84) * mm, "end": v(-12.97, -21.37) * mm});
            skLineSegment(sketch, "E11.182.1", {"start": v(-13.82, -20.84) * mm, "end": v(-13.86, -21.84) * mm});
            skLineSegment(sketch, "E11.183.0", {"start": v(-13.16, -22.26) * mm, "end": v(-12.3, -21.77) * mm});
            skLineSegment(sketch, "E11.183.1", {"start": v(-13.15, -21.26) * mm, "end": v(-13.16, -22.26) * mm});
            skLineSegment(sketch, "E11.184.0", {"start": v(-12.46, -22.66) * mm, "end": v(-11.6, -22.14) * mm});
            skLineSegment(sketch, "E11.184.1", {"start": v(-12.48, -21.66) * mm, "end": v(-12.46, -22.66) * mm});
            skLineSegment(sketch, "E11.185.0", {"start": v(-11.74, -23.04) * mm, "end": v(-10.9, -22.5) * mm});
            skLineSegment(sketch, "E11.185.1", {"start": v(-11.8, -22.04) * mm, "end": v(-11.74, -23.04) * mm});
            skLineSegment(sketch, "E11.186.0", {"start": v(-11.01, -23.4) * mm, "end": v(-10.19, -22.83) * mm});
            skLineSegment(sketch, "E11.186.1", {"start": v(-11.1, -22.4) * mm, "end": v(-11.01, -23.4) * mm});
            skLineSegment(sketch, "E11.187.0", {"start": v(-10.27, -23.73) * mm, "end": v(-9.47, -23.14) * mm});
            skLineSegment(sketch, "E11.187.1", {"start": v(-10.39, -22.74) * mm, "end": v(-10.27, -23.73) * mm});
            skLineSegment(sketch, "E11.188.0", {"start": v(-9.52, -24.04) * mm, "end": v(-8.74, -23.42) * mm});
            skLineSegment(sketch, "E11.188.1", {"start": v(-9.67, -23.06) * mm, "end": v(-9.52, -24.04) * mm});
            skLineSegment(sketch, "E11.189.0", {"start": v(-8.76, -24.33) * mm, "end": v(-8, -23.69) * mm});
            skLineSegment(sketch, "E11.189.1", {"start": v(-8.94, -23.35) * mm, "end": v(-8.76, -24.33) * mm});
            skLineSegment(sketch, "E11.190.0", {"start": v(-8, -24.6) * mm, "end": v(-7.25, -23.93) * mm});
            skLineSegment(sketch, "E11.190.1", {"start": v(-8.2, -23.62) * mm, "end": v(-8, -24.6) * mm});
            skLineSegment(sketch, "E11.191.0", {"start": v(-7.21, -24.83) * mm, "end": v(-6.5, -24.14) * mm});
            skLineSegment(sketch, "E11.191.1", {"start": v(-7.45, -23.86) * mm, "end": v(-7.21, -24.83) * mm});
            skLineSegment(sketch, "E11.192.0", {"start": v(-6.43, -25.05) * mm, "end": v(-5.73, -24.33) * mm});
            skLineSegment(sketch, "E11.192.1", {"start": v(-6.7, -24.09) * mm, "end": v(-6.43, -25.05) * mm});
            skLineSegment(sketch, "E11.193.0", {"start": v(-5.64, -25.24) * mm, "end": v(-4.96, -24.5) * mm});
            skLineSegment(sketch, "E11.193.1", {"start": v(-5.94, -24.28) * mm, "end": v(-5.64, -25.24) * mm});
            skLineSegment(sketch, "E11.194.0", {"start": v(-4.85, -25.4) * mm, "end": v(-4.2, -24.65) * mm});
            skLineSegment(sketch, "E11.194.1", {"start": v(-5.17, -24.46) * mm, "end": v(-4.85, -25.4) * mm});
            skLineSegment(sketch, "E11.195.0", {"start": v(-4.05, -25.54) * mm, "end": v(-3.42, -24.77) * mm});
            skLineSegment(sketch, "E11.195.1", {"start": v(-4.4, -24.6) * mm, "end": v(-4.05, -25.54) * mm});
            skLineSegment(sketch, "E11.196.0", {"start": v(-3.24, -25.66) * mm, "end": v(-2.64, -24.86) * mm});
            skLineSegment(sketch, "E11.196.1", {"start": v(-3.63, -24.74) * mm, "end": v(-3.24, -25.66) * mm});
            skLineSegment(sketch, "E11.197.0", {"start": v(-2.43, -25.75) * mm, "end": v(-1.85, -24.93) * mm});
            skLineSegment(sketch, "E11.197.1", {"start": v(-2.85, -24.84) * mm, "end": v(-2.43, -25.75) * mm});
            skLineSegment(sketch, "E11.198.0", {"start": v(-1.62, -25.8) * mm, "end": v(-1.07, -24.98) * mm});
            skLineSegment(sketch, "E11.198.1", {"start": v(-2.07, -24.91) * mm, "end": v(-1.62, -25.8) * mm});
            skLineSegment(sketch, "E11.199.0", {"start": v(-0.81, -25.85) * mm, "end": v(-0.29, -25) * mm});
            skLineSegment(sketch, "E11.199.1", {"start": v(-1.28, -24.97) * mm, "end": v(-0.81, -25.85) * mm});
            skSolve(sketch);
        }
        {
            var Q0;
            Q0=makeQuery(id+"F0.imprint","IMPRINT",FACE,{"disambiguationData":[TD([[makeQuery(id+"F0.imprint","IMPRINT",EDGE,{"derivedFrom":sQuery(id+"F0.wireOp",EDGE,"E0")}),-1.0]])]});
            var Q1;
            {var subQ0=sQuery(id+"F0.wireOp",EDGE,"E2");Q1=makeQuery(id+"F0.imprint","IMPRINT",FACE,{"disambiguationData":[TD([[makeQuery(id+"F0.imprint","IMPRINT",EDGE,{"derivedFrom":subQ0}),-1.0]])]});}
            var Q2;
            {var subQ0=sQuery(id+"F0.wireOp",EDGE,"E3");Q2=makeQuery(id+"F0.imprint","IMPRINT",FACE,{"disambiguationData":[TD([[makeQuery(id+"F0.imprint","IMPRINT",EDGE,{"derivedFrom":subQ0}),1.0]])]});}
            var Q3;
            {var subQ0=sQuery(id+"F0.wireOp",EDGE,"E6.1.0");Q3=makeQuery(id+"F0.imprint","IMPRINT",FACE,{"disambiguationData":[TD([[makeQuery(id+"F0.imprint","IMPRINT",EDGE,{"derivedFrom":subQ0}),1.0]])]});}
            var Q4;
            {var subQ0=sQuery(id+"F0.wireOp",EDGE,"E6.2.0");Q4=makeQuery(id+"F0.imprint","IMPRINT",FACE,{"disambiguationData":[TD([[makeQuery(id+"F0.imprint","IMPRINT",EDGE,{"derivedFrom":subQ0}),1.0]])]});}
            var Q5;
            Q5=makeQuery(id+"F0.imprint","IMPRINT",FACE,{"disambiguationData":[TD([[makeQuery(id+"F0.imprint","IMPRINT",EDGE,{"derivedFrom":sQuery(id+"F0.wireOp",EDGE,"E1")}),1.0]])]});
            var Q6;
            {var subQ805=sQuery(id+"F0.wireOp",EDGE,"E5");var subQ843=makeQuery(id+"F0.imprint","INTERSECT",VERTEX,{"derivedFrom":[subQ805,sQuery(id+"F0.wireOp",EDGE,"E6.1.0")]});Q6=makeQuery(id+"F0.imprint","IMPRINT",FACE,{"disambiguationData":[TD([[makeQuery(id+"F0.imprint","IMPRINT",EDGE,{"disambiguationData":[TD([[subQ843,-1.0]])],"derivedFrom":subQ805}),-1.0]])]});}
            extrude(context, id + "F1", {"entities" : qUnion([Q0, Q1, Q2, Q3, Q4, Q5, Q6]), "depth" : 6.35 * mm});
        }
    });
